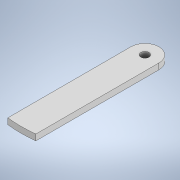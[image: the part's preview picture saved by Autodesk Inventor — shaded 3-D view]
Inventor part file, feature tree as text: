
AUTODESK INVENTOR PART (.ipt)
format: ipt  version: 2021 (Build 250183000, 183)  size: 113,664 bytes
history: native  units: mm
features: sketch x4, extrude x3, projected_geometry x3
ambient origin geometry x8: Origin, YZ Plane, XZ Plane, XY Plane, X Axis, Y Axis, Z Axis, Center Point
bodies: Solid1 (feature_tree)
feature tree (10):
  extrude  "Extrusion1"  Depth=9.398mm
  extrude  "Extrusion2"  Depth=2.0mm
  extrude  "Extrusion3"  Depth=0.1mm TaperAngle=0.0deg
  sketch  "Sketch4"
  sketch  "Sketch1"  dims[d0=83.083mm d1=9.398mm]
  sketch  "Sketch2"  dims[d2=2.0mm d3=0.0mm d4=2.75mm]
  sketch  "Sketch3"  dims[d5=0.0mm d6=0.0mm d7=0.1mm d8=0.0mm]
  projected_geometry  "Projected Loop1"
  projected_geometry  "Projected Loop2"
  projected_geometry  "Projected Loop3"
